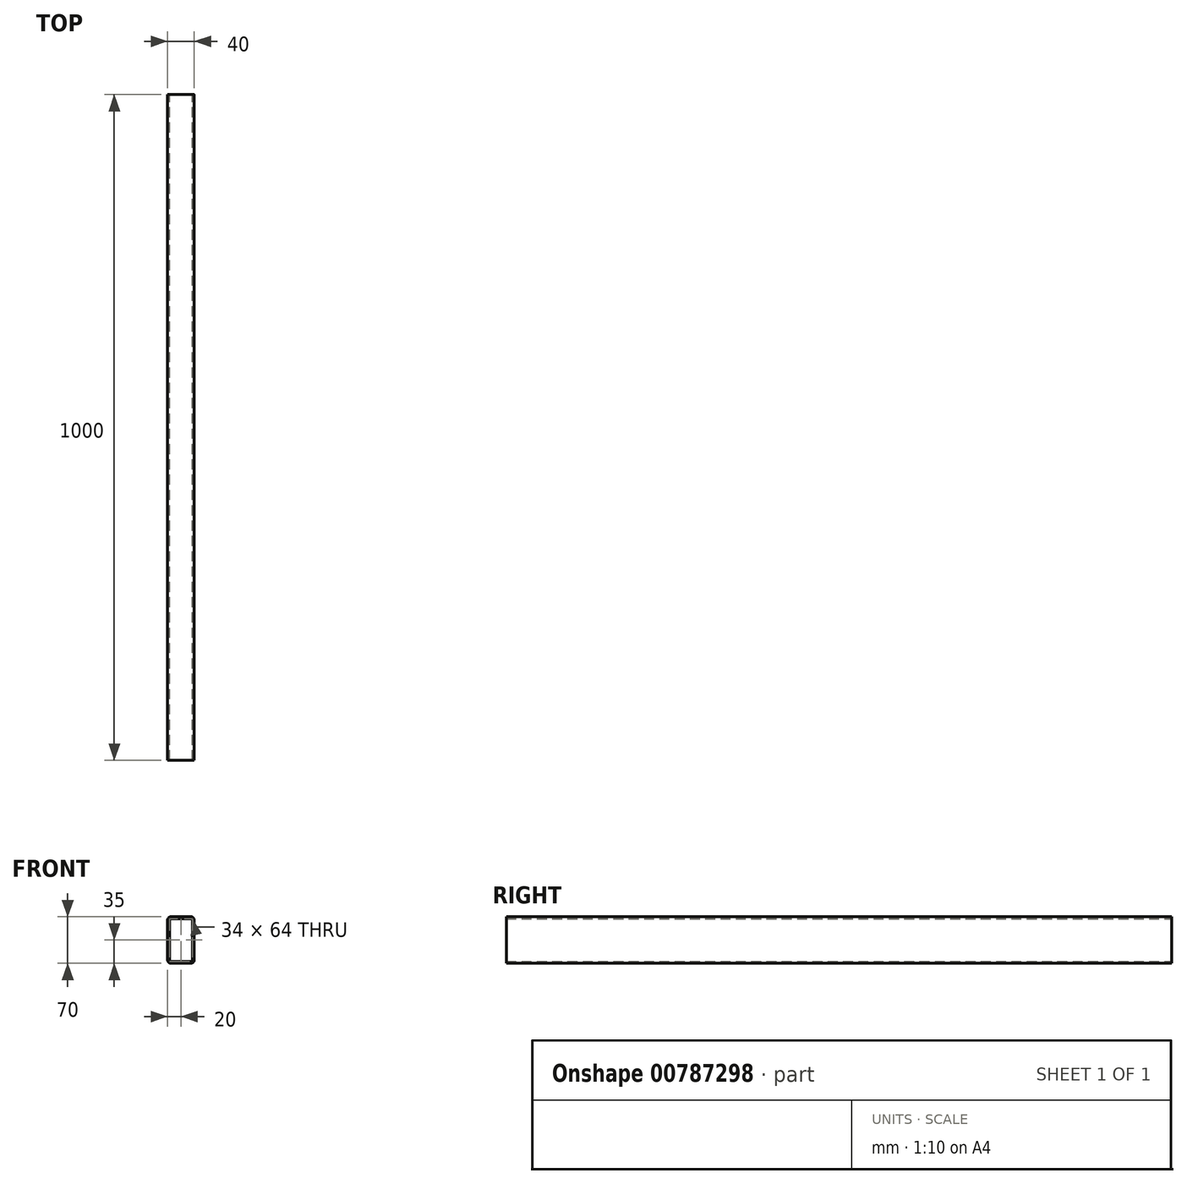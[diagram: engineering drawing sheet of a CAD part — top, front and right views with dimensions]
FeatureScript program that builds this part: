
annotation { "Feature Type Name" : "Feature", "Feature Type Description" : "" }
export const myFeature = defineFeature(function(context is Context, id is Id, definition is map)
    precondition{}
    {
        {
            var Q0;
            Q0=qCreatedBy(makeId("Front.planeOp"),FACE);
            var sketch = newSketch(context, id + "F0", { "sketchPlane" : qUnion([Q0])});
            skLineSegment(sketch, "E0.bottom", {"start": v(15, 35) * mm, "end": v(-15, 35) * mm});
            skLineSegment(sketch, "E0.top", {"start": v(15, -35) * mm, "end": v(-15, -35) * mm});
            skLineSegment(sketch, "E0.left", {"start": v(20, 30) * mm, "end": v(20, -30) * mm});
            skLineSegment(sketch, "E0.right", {"start": v(-20, 30) * mm, "end": v(-20, -30) * mm});
            skPoint(sketch, "E0.middle", {"position": v(0, 0) * mm});
            skPoint(sketch, "E1.visualSharp", {"position": v(-20, 35) * mm});
            skArc(sketch, "E1.filletArc", {"start": v(-15, 35) * mm, "mid": v(-18.54, 33.54) * mm, "end": v(-20, 30) * mm});
            skPoint(sketch, "E2.visualSharp", {"position": v(20, 35) * mm});
            skArc(sketch, "E2.filletArc", {"start": v(20, 30) * mm, "mid": v(18.54, 33.54) * mm, "end": v(15, 35) * mm});
            skPoint(sketch, "E3.visualSharp", {"position": v(20, -35) * mm});
            skArc(sketch, "E3.filletArc", {"start": v(15, -35) * mm, "mid": v(18.54, -33.54) * mm, "end": v(20, -30) * mm});
            skPoint(sketch, "E4.visualSharp", {"position": v(-20, -35) * mm});
            skArc(sketch, "E4.filletArc", {"start": v(-20, -30) * mm, "mid": v(-18.54, -33.54) * mm, "end": v(-15, -35) * mm});
            skLineSegment(sketch, "E5.0", {"start": v(-17, 32) * mm, "end": v(-17, -32) * mm});
            skLineSegment(sketch, "E5.1", {"start": v(17, 32) * mm, "end": v(-17, 32) * mm});
            skLineSegment(sketch, "E5.2", {"start": v(17, 32) * mm, "end": v(17, -32) * mm});
            skLineSegment(sketch, "E5.3", {"start": v(17, -32) * mm, "end": v(-17, -32) * mm});
            skSolve(sketch);
        }
        {
            var Q0;
            Q0=makeQuery(id+"F0.imprint","IMPRINT",FACE,{"disambiguationData":[TD([[makeQuery(id+"F0.imprint","IMPRINT",EDGE,{"derivedFrom":sQuery(id+"F0.wireOp",EDGE,"E0.bottom")}),1.0]])]});
            extrude(context, id + "F1", {"entities" : qUnion([Q0]), "depth" : 1000 * mm, "offsetDistance" : 25 * mm});
        }
    });
